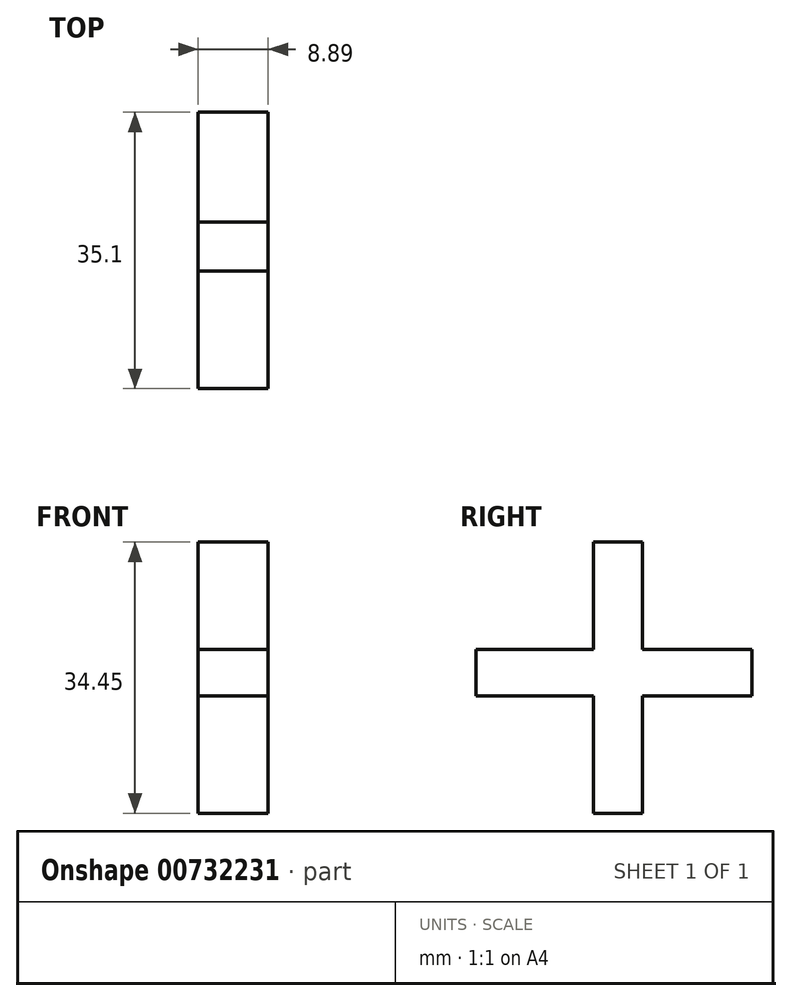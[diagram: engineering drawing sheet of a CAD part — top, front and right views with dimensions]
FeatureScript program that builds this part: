
annotation { "Feature Type Name" : "Feature", "Feature Type Description" : "" }
export const myFeature = defineFeature(function(context is Context, id is Id, definition is map)
    precondition{}
    {
        {
            var Q0;
            Q0=qCreatedBy(makeId("Right.planeOp"),FACE);
            var sketch = newSketch(context, id + "F0", { "sketchPlane" : qUnion([Q0])});
            skLineSegment(sketch, "E0.bottom", {"start": v(-2.88, 16.48) * mm, "end": v(3.36, 16.48) * mm});
            skLineSegment(sketch, "E0.top", {"start": v(-2.88, -17.97) * mm, "end": v(3.36, -17.97) * mm});
            skLineSegment(sketch, "E0.left", {"start": v(-2.88, 16.48) * mm, "end": v(-2.88, -17.97) * mm});
            skLineSegment(sketch, "E0.right", {"start": v(3.36, 16.48) * mm, "end": v(3.36, -17.97) * mm});
            skLineSegment(sketch, "E1.bottom", {"start": v(-17.8, 2.86) * mm, "end": v(17.3, 2.86) * mm});
            skLineSegment(sketch, "E1.top", {"start": v(-17.8, -3.05) * mm, "end": v(17.3, -3.05) * mm});
            skLineSegment(sketch, "E1.left", {"start": v(-17.8, 2.86) * mm, "end": v(-17.8, -3.05) * mm});
            skLineSegment(sketch, "E1.right", {"start": v(17.3, 2.86) * mm, "end": v(17.3, -3.05) * mm});
            skSolve(sketch);
        }
        {
            var Q0;
            Q0 = qSketchRegion(id + "F0", true);
            extrude(context, id + "F1", {"entities" : qUnion([Q0]), "depth" : 8.9 * mm, "offsetDistance" : 25.4 * mm});
        }
    });
